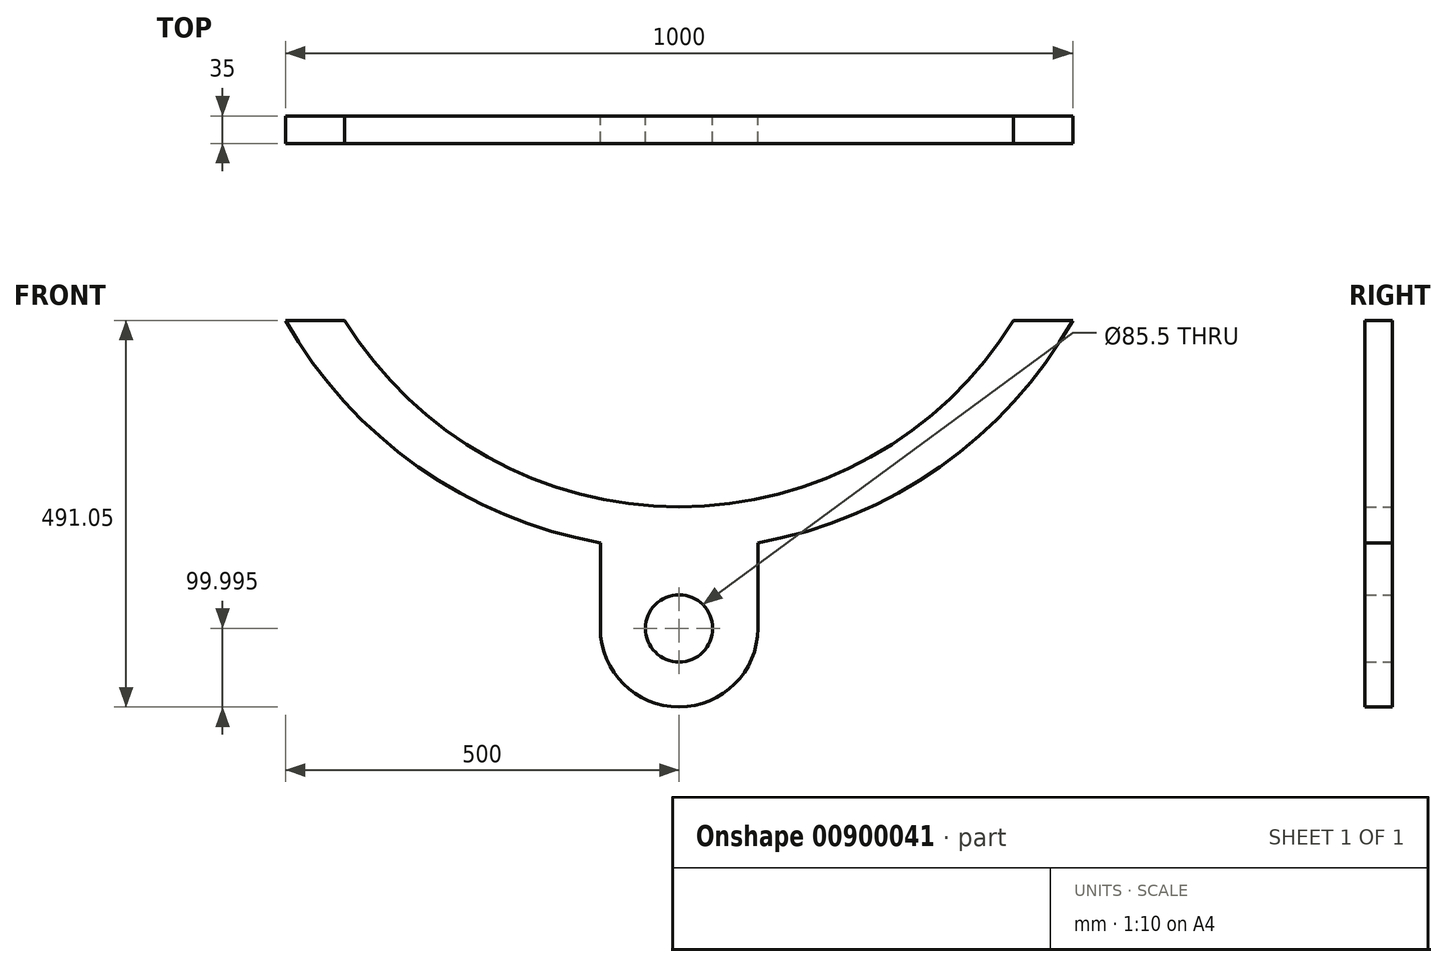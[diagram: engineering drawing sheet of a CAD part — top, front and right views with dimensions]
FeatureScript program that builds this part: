
annotation { "Feature Type Name" : "Feature", "Feature Type Description" : "" }
export const myFeature = defineFeature(function(context is Context, id is Id, definition is map)
    precondition{}
    {
        {
            var Q0;
            Q0=qCreatedBy(makeId("Front.planeOp"),FACE);
            var sketch = newSketch(context, id + "F0", { "sketchPlane" : qUnion([Q0])});
            skArc(sketch, "E0", {"start": v(0, 0) * mm, "mid": v(168.45, -185.84) * mm, "end": v(400, -282.3) * mm});
            skArc(sketch, "E1", {"start": v(75, 0) * mm, "mid": v(500, -236.6) * mm, "end": v(925, 0) * mm});
            skArc(sketch, "E2", {"start": v(400, -391.05) * mm, "mid": v(500, -491.05) * mm, "end": v(600, -391.05) * mm});
            skPoint(sketch, "E2.centerSnap0", {"position": v(500, -291.05) * mm});
            skLineSegment(sketch, "E3", {"start": v(400, -391.05) * mm, "end": v(400, -282.3) * mm});
            skLineSegment(sketch, "E4", {"start": v(600, -391.05) * mm, "end": v(600, -282.3) * mm});
            skArc(sketch, "E5.trimOffspring", {"start": v(600, -282.3) * mm, "mid": v(831.55, -185.84) * mm, "end": v(1000, 0) * mm});
            skCircle(sketch, "E6", {"center": v(500, -391.05) * mm, "radius": 42.75 * mm});
            skLineSegment(sketch, "E7", {"start": v(0, 0) * mm, "end": v(75, 0) * mm});
            skLineSegment(sketch, "E8", {"start": v(925, 0) * mm, "end": v(1000, 0) * mm});
            skSolve(sketch);
        }
        {
            var Q0;
            Q0=makeQuery(id+"F0.imprint","IMPRINT",FACE,{"disambiguationData":[TD([[makeQuery(id+"F0.imprint","IMPRINT",EDGE,{"derivedFrom":sQuery(id+"F0.wireOp",EDGE,"E0")}),1.0]])]});
            extrude(context, id + "F1", {"entities" : qUnion([Q0]), "depth" : 35 * mm, "offsetDistance" : 25 * mm});
        }
    });
